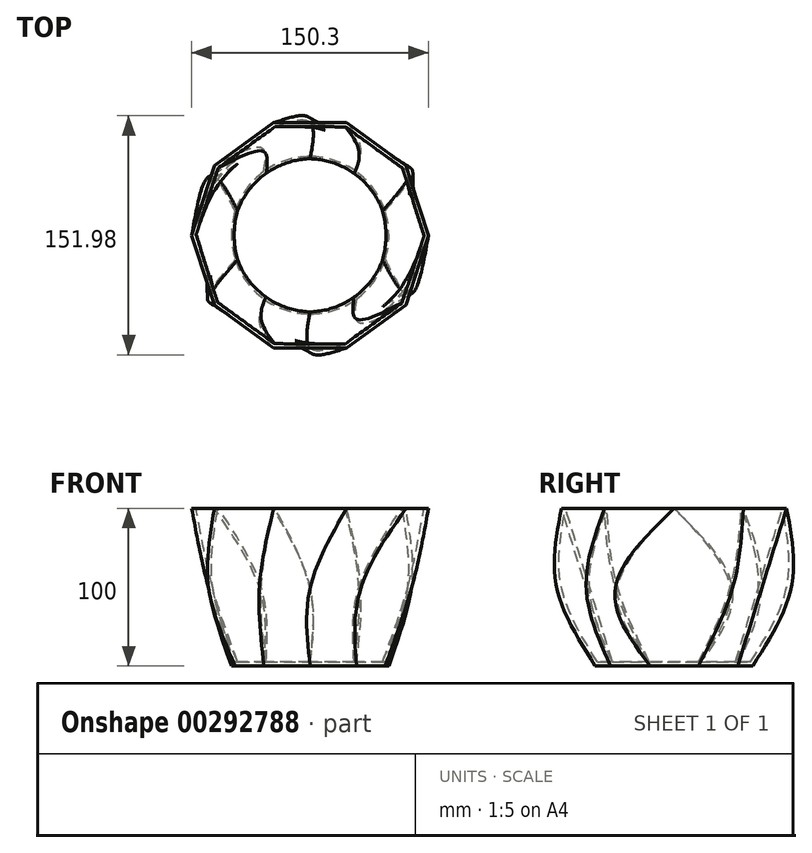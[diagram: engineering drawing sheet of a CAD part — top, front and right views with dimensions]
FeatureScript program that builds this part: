
annotation { "Feature Type Name" : "Feature", "Feature Type Description" : "" }
export const myFeature = defineFeature(function(context is Context, id is Id, definition is map)
    precondition{}
    {
        {
            var Q0;
            Q0=qCreatedBy(makeId("Top.planeOp"),FACE);
            var sketch = newSketch(context, id + "F0", { "sketchPlane" : qUnion([Q0])});
            skCircle(sketch, "E0", {"center": v(0, 0) * mm, "radius": 50 * mm});
            skSolve(sketch);
        }
        {
            var Q0;
            Q0=qCreatedBy(makeId("Top.planeOp"),FACE);
            cPlane(context, id + "F1", {"entities" : qUnion([Q0]), "cplaneType" : CPlaneType.OFFSET, "offset" : 50 * mm, "width" : 150 * mm, "height" : 150 * mm});
        }
        {
            var Q0;
            Q0=qCreatedBy(id+"F1.planeOp",FACE);
            cPlane(context, id + "F2", {"entities" : qUnion([Q0]), "cplaneType" : CPlaneType.OFFSET, "offset" : 50 * mm, "width" : 150 * mm, "height" : 150 * mm});
        }
        {
            var Q0;
            Q0=qCreatedBy(id+"F1.planeOp",FACE);
            var sketch = newSketch(context, id + "F3", { "sketchPlane" : qUnion([Q0])});
            skCircle(sketch, "E1.cCircle", {"center": v(0, 0) * mm, "radius": 64.53 * mm, "construction": true});
            skLineSegment(sketch, "E1.0", {"start": v(-0.13, 74.52) * mm, "end": v(64.47, 37.37) * mm});
            skLineSegment(sketch, "E1.1", {"start": v(64.47, 37.37) * mm, "end": v(64.6, -37.15) * mm});
            skLineSegment(sketch, "E1.2", {"start": v(64.6, -37.15) * mm, "end": v(0.13, -74.52) * mm});
            skLineSegment(sketch, "E1.3", {"start": v(0.13, -74.52) * mm, "end": v(-64.47, -37.37) * mm});
            skLineSegment(sketch, "E1.4", {"start": v(-64.47, -37.37) * mm, "end": v(-64.6, 37.15) * mm});
            skLineSegment(sketch, "E1.5", {"start": v(-64.6, 37.15) * mm, "end": v(-0.13, 74.52) * mm});
            skPoint(sketch, "E1.0.midPoint", {"position": v(32.17, 55.94) * mm});
            skSolve(sketch);
        }
        {
            var Q0;
            Q0=qCreatedBy(id+"F2.planeOp",FACE);
            var sketch = newSketch(context, id + "F4", { "sketchPlane" : qUnion([Q0])});
            skCircle(sketch, "E2.cCircle", {"center": v(0, 0) * mm, "radius": 75.15 * mm, "construction": true});
            skLineSegment(sketch, "E2.0", {"start": v(75.15, 0) * mm, "end": v(60.8, -44.17) * mm});
            skLineSegment(sketch, "E2.1", {"start": v(60.8, -44.17) * mm, "end": v(23.22, -71.47) * mm});
            skLineSegment(sketch, "E2.2", {"start": v(23.22, -71.47) * mm, "end": v(-23.22, -71.47) * mm});
            skLineSegment(sketch, "E2.3", {"start": v(-23.22, -71.47) * mm, "end": v(-60.8, -44.17) * mm});
            skLineSegment(sketch, "E2.4", {"start": v(-60.8, -44.17) * mm, "end": v(-75.15, 0) * mm});
            skLineSegment(sketch, "E2.5", {"start": v(-75.15, 0) * mm, "end": v(-60.8, 44.17) * mm});
            skLineSegment(sketch, "E2.6", {"start": v(-60.8, 44.17) * mm, "end": v(-23.22, 71.47) * mm});
            skLineSegment(sketch, "E2.7", {"start": v(-23.22, 71.47) * mm, "end": v(23.22, 71.47) * mm});
            skLineSegment(sketch, "E2.8", {"start": v(23.22, 71.47) * mm, "end": v(60.8, 44.17) * mm});
            skLineSegment(sketch, "E2.9", {"start": v(60.8, 44.17) * mm, "end": v(75.15, 0) * mm});
            skSolve(sketch);
        }
        {
            var Q0;
            Q0=makeQuery(id+"F0.imprint","IMPRINT",FACE,{"disambiguationData":[TD([[makeQuery(id+"F0.imprint","IMPRINT",EDGE,{"derivedFrom":sQuery(id+"F0.wireOp",EDGE,"E0")}),1.0]])]});
            var Q1;
            Q1=makeQuery(id+"F3.imprint","IMPRINT",FACE,{"disambiguationData":[TD([[makeQuery(id+"F3.imprint","IMPRINT",EDGE,{"derivedFrom":sQuery(id+"F3.wireOp",EDGE,"E1.0")}),-1.0]])]});
            var Q2;
            Q2=makeQuery(id+"F4.imprint","IMPRINT",FACE,{"disambiguationData":[TD([[makeQuery(id+"F4.imprint","IMPRINT",EDGE,{"derivedFrom":sQuery(id+"F4.wireOp",EDGE,"E2.0")}),-1.0]])]});
            loft(context, id + "F5", {"sheetProfilesArray" : [{ "sheetProfileEntities" : qUnion([Q0]) }, { "sheetProfileEntities" : qUnion([Q1]) }, { "sheetProfileEntities" : qUnion([Q2]) }]});
        }
        {
            var Q0;
            Q0=makeQuery(id+"F5.opLoft","CAP_FACE",FACE,{"disambiguationData":[OSD([makeQuery(id+"F4.imprint","IMPRINT",FACE,{"disambiguationData":[TD([[makeQuery(id+"F4.imprint","IMPRINT",EDGE,{"derivedFrom":sQuery(id+"F4.wireOp",EDGE,"E2.0")}),-1.0]])]})])],"isStart":true});
            shell(context, id + "F6", {"entities" : qUnion([Q0]), "thickness" : 2.5 * mm});
        }
    });
